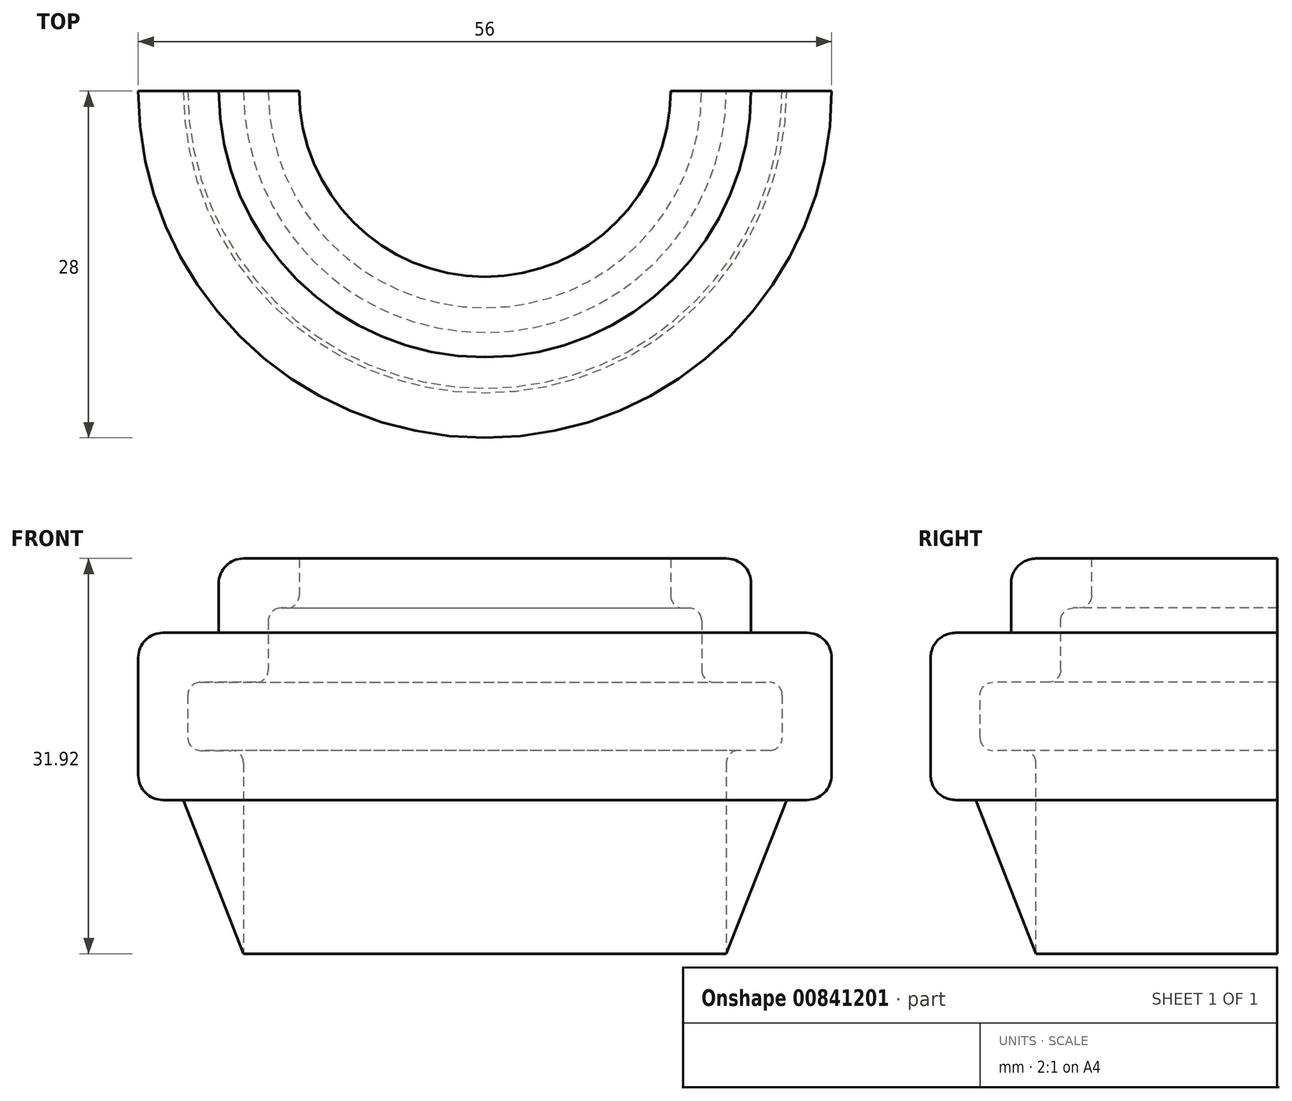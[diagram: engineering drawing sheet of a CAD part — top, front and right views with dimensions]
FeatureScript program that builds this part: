
annotation { "Feature Type Name" : "Feature", "Feature Type Description" : "" }
export const myFeature = defineFeature(function(context is Context, id is Id, definition is map)
    precondition{}
    {
        {
            var Q0;
            Q0=qCreatedBy(makeId("Front.planeOp"),FACE);
            var sketch = newSketch(context, id + "F0", { "sketchPlane" : qUnion([Q0])});
            skLineSegment(sketch, "E0", {"start": v(15, 15.92) * mm, "end": v(15, 11.92) * mm});
            skLineSegment(sketch, "E1", {"start": v(15, 11.92) * mm, "end": v(17.5, 11.92) * mm});
            skLineSegment(sketch, "E2", {"start": v(17.5, 11.92) * mm, "end": v(17.5, 5.92) * mm});
            skLineSegment(sketch, "E3", {"start": v(17.5, 5.92) * mm, "end": v(24, 5.92) * mm});
            skLineSegment(sketch, "E4", {"start": v(24, 5.92) * mm, "end": v(24, 0.42) * mm});
            skLineSegment(sketch, "E5", {"start": v(24, 0.42) * mm, "end": v(19.5, 0.42) * mm});
            skLineSegment(sketch, "E6", {"start": v(21.5, 15.92) * mm, "end": v(15, 15.92) * mm});
            skLineSegment(sketch, "E7", {"start": v(28, -3.58) * mm, "end": v(24.36, -3.58) * mm});
            skLineSegment(sketch, "E8", {"start": v(24.36, -3.58) * mm, "end": v(19.5, -16) * mm});
            skLineSegment(sketch, "E9", {"start": v(0, 4.7) * mm, "end": v(0, -55) * mm});
            skLineSegment(sketch, "E10", {"start": v(19.5, 0.42) * mm, "end": v(19.5, -16) * mm});
            skLineSegment(sketch, "E11", {"start": v(28, -3.58) * mm, "end": v(28, 9.92) * mm});
            skLineSegment(sketch, "E12", {"start": v(28, 9.92) * mm, "end": v(21.5, 9.92) * mm});
            skLineSegment(sketch, "E13", {"start": v(21.5, 9.92) * mm, "end": v(21.5, 15.92) * mm});
            skSolve(sketch);
        }
        {
            var Q0;
            Q0 = qSketchRegion(id + "F0", true);
            var Q1;
            Q1=sQuery(id+"F0.wireOp",EDGE,"E9");
            revolve(context, id + "F1", {"surfaceOperationType" : NewSurfaceOperationType.NEW, "entities" : qUnion([Q0]), "axis" : qUnion([Q1]), "revolveType" : RevolveType.ONE_DIRECTION, "angle" : 180 * degree});
        }
        {
            var Q0;
            Q0=makeQuery(id+"F1.opRevolve","SWEPT_EDGE",EDGE,{"disambiguationData":[OSD([sQuery(id+"F0.wireOp",EDGE,"E1"),sQuery(id+"F0.wireOp",EDGE,"E2")])]});
            var Q1;
            Q1=makeQuery(id+"F1.opRevolve","SWEPT_EDGE",EDGE,{"disambiguationData":[OSD([sQuery(id+"F0.wireOp",EDGE,"E2"),sQuery(id+"F0.wireOp",EDGE,"E3")])]});
            var Q2;
            Q2=makeQuery(id+"F1.opRevolve","SWEPT_EDGE",EDGE,{"disambiguationData":[OSD([sQuery(id+"F0.wireOp",EDGE,"E5"),sQuery(id+"F0.wireOp",EDGE,"E10")])]});
            var Q3;
            Q3=makeQuery(id+"F1.opRevolve","SWEPT_EDGE",EDGE,{"disambiguationData":[OSD([sQuery(id+"F0.wireOp",EDGE,"E3"),sQuery(id+"F0.wireOp",EDGE,"E4")])]});
            var Q4;
            Q4=makeQuery(id+"F1.opRevolve","SWEPT_EDGE",EDGE,{"disambiguationData":[OSD([sQuery(id+"F0.wireOp",EDGE,"E0"),sQuery(id+"F0.wireOp",EDGE,"E1")])]});
            var Q5;
            Q5=makeQuery(id+"F1.opRevolve","SWEPT_EDGE",EDGE,{"disambiguationData":[OSD([sQuery(id+"F0.wireOp",EDGE,"E4"),sQuery(id+"F0.wireOp",EDGE,"E5")])]});
            fillet(context, id + "F2", {"entities" : qUnion([Q0, Q1, Q2, Q3, Q4, Q5]), "radius" : 1 * mm, "tangentPropagation" : true, "allowEdgeOverflow" : false});
        }
        {
            var Q0;
            Q0=makeQuery(id+"F1.opRevolve","SWEPT_EDGE",EDGE,{"disambiguationData":[OSD([sQuery(id+"F0.wireOp",EDGE,"E7"),sQuery(id+"F0.wireOp",EDGE,"E11")])]});
            var Q1;
            Q1=makeQuery(id+"F1.opRevolve","SWEPT_EDGE",EDGE,{"disambiguationData":[OSD([sQuery(id+"F0.wireOp",EDGE,"E11"),sQuery(id+"F0.wireOp",EDGE,"E12")])]});
            var Q2;
            Q2=makeQuery(id+"F1.opRevolve","SWEPT_EDGE",EDGE,{"disambiguationData":[OSD([sQuery(id+"F0.wireOp",EDGE,"E6"),sQuery(id+"F0.wireOp",EDGE,"E13")])]});
            fillet(context, id + "F3", {"entities" : qUnion([Q0, Q1, Q2]), "radius" : 2 * mm, "tangentPropagation" : true, "allowEdgeOverflow" : false});
        }
    });
